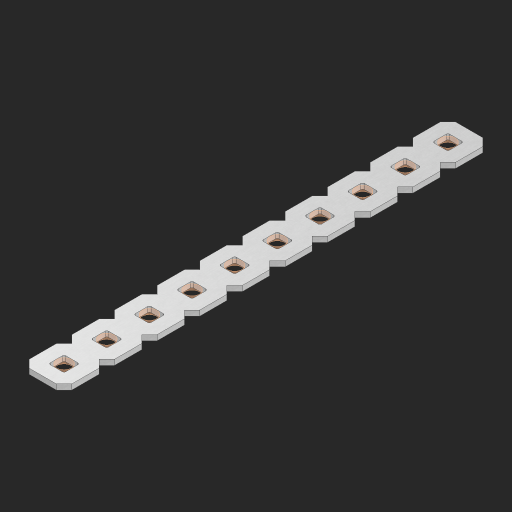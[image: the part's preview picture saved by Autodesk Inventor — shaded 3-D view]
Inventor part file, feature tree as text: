
AUTODESK INVENTOR PART (.ipt)
format: ipt  version: 2023 (Build 270158000, 158)  size: 372,736 bytes
history: native  units: in
note: dims shown in document units (in); Inventor stores cm internally (conversion verified against a paired STEP export)
features: other x11, extrude x9, sketch x2, pattern_linear x1
ambient origin geometry x8: Origin, YZ Plane, XZ Plane, XY Plane, X Axis, Y Axis, Z Axis, Center Point
bodies: Solid1 (feature_tree), Body (feature_tree)
feature tree (23):
  pattern_linear  "Rectangular Pattern1"  Spacing1=0.09in  [1 undecoded]
  sketch  "Sketch1"  dims[d1=0.5in]
  sketch  "Sketch2"  dims[d2=0.182in d3=0.09in d4=0.09in d5=0.09in d6=0.09in d7=0.09in d8=0.09in d9=0.09in d10=0.09in d11=0.02in d13=0.0in d14=0.172in d15=0.0625in d16=0.0in d19=0.5in d22=0.5in]
  other  "Srf1"
  other  "Srf126"
  other  "Srf127"
  other  "Srf128"
  other  "Srf129"
  other  "Srf130"
  other  "Srf131"
  other  "Srf250"
  other  "Srf251"
  other  "Srf252"
  other  "Circle"
  extrude  "ExtrusionSrf126"  Depth=0.09in
  extrude  "ExtrusionSrf127"  Depth=0.09in
  extrude  "ExtrusionSrf128"  Depth=0.09in
  extrude  "ExtrusionSrf129"  Depth=0.09in
  extrude  "ExtrusionSrf130"  Depth=0.09in
  extrude  "ExtrusionSrf131"  Depth=0.09in
  extrude  "ExtrusionSrf250"  Depth=0.09in
  extrude  "ExtrusionSrf251"  Depth=0.02in
  extrude  "ExtrusionSrf252"  TaperAngle=0.0deg  [1 undecoded]
note: 2 required parameter values undecoded (feature->parameter linkage not recoverable at this tier; creation-order binding heuristic only, values carry confidence <= 0.55)
